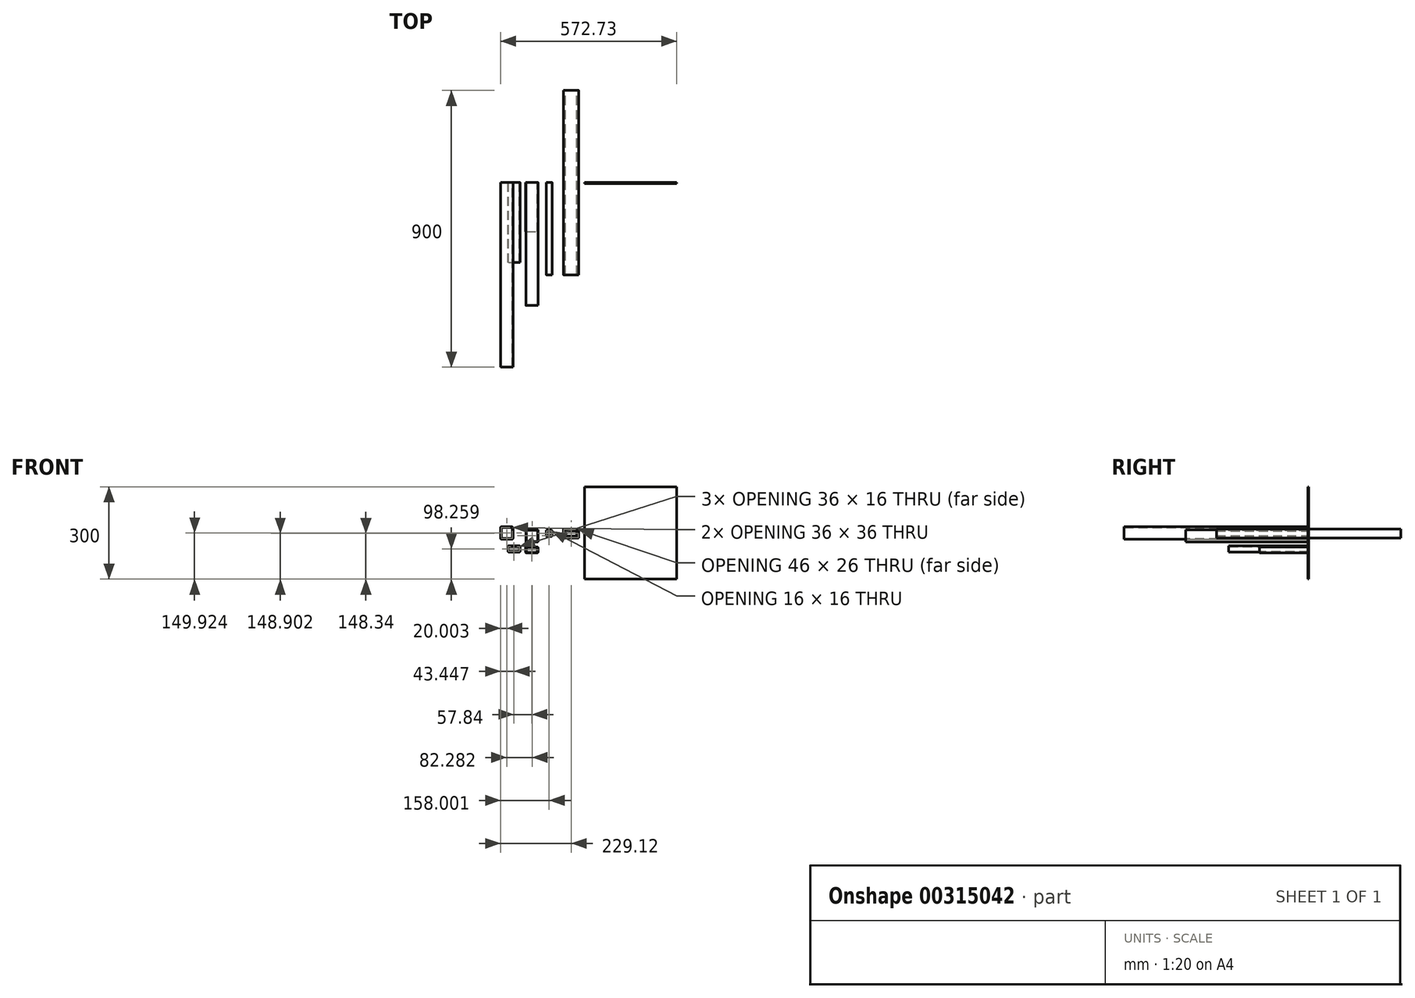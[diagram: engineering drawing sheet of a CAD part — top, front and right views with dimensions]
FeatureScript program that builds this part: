
annotation { "Feature Type Name" : "Feature", "Feature Type Description" : "" }
export const myFeature = defineFeature(function(context is Context, id is Id, definition is map)
    precondition{}
    {
        {
            var Q0;
            Q0=qCreatedBy(makeId("Front.planeOp"),FACE);
            var sketch = newSketch(context, id + "F0", { "sketchPlane" : qUnion([Q0])});
            skLineSegment(sketch, "E0.bottom", {"start": v(22.5, 15) * mm, "end": v(-22.5, 15) * mm});
            skLineSegment(sketch, "E0.top", {"start": v(22.5, -15) * mm, "end": v(-22.5, -15) * mm});
            skLineSegment(sketch, "E0.left", {"start": v(25, 12.5) * mm, "end": v(25, -12.5) * mm});
            skLineSegment(sketch, "E0.right", {"start": v(-25, 12.5) * mm, "end": v(-25, -12.5) * mm});
            skPoint(sketch, "E0.middle", {"position": v(0, 0) * mm});
            skPoint(sketch, "E1.visualSharp", {"position": v(-25, 15) * mm});
            skArc(sketch, "E1.filletArc", {"start": v(-22.5, 15) * mm, "mid": v(-24.27, 14.27) * mm, "end": v(-25, 12.5) * mm});
            skPoint(sketch, "E2.visualSharp", {"position": v(25, 15) * mm});
            skArc(sketch, "E2.filletArc", {"start": v(25, 12.5) * mm, "mid": v(24.27, 14.27) * mm, "end": v(22.5, 15) * mm});
            skPoint(sketch, "E3.visualSharp", {"position": v(25, -15) * mm});
            skArc(sketch, "E3.filletArc", {"start": v(22.5, -15) * mm, "mid": v(24.27, -14.27) * mm, "end": v(25, -12.5) * mm});
            skPoint(sketch, "E4.visualSharp", {"position": v(-25, -15) * mm});
            skArc(sketch, "E4.filletArc", {"start": v(-25, -12.5) * mm, "mid": v(-24.27, -14.27) * mm, "end": v(-22.5, -15) * mm});
            skLineSegment(sketch, "E5.0", {"start": v(22.5, 13) * mm, "end": v(-22.5, 13) * mm});
            skArc(sketch, "E5.1", {"start": v(23, 12.5) * mm, "mid": v(22.85, 12.85) * mm, "end": v(22.5, 13) * mm});
            skArc(sketch, "E5.2", {"start": v(-22.5, 13) * mm, "mid": v(-22.85, 12.85) * mm, "end": v(-23, 12.5) * mm});
            skLineSegment(sketch, "E5.3", {"start": v(23, 12.5) * mm, "end": v(23, -12.5) * mm});
            skLineSegment(sketch, "E5.4", {"start": v(-23, 12.5) * mm, "end": v(-23, -12.5) * mm});
            skArc(sketch, "E5.5", {"start": v(-23, -12.5) * mm, "mid": v(-22.85, -12.85) * mm, "end": v(-22.5, -13) * mm});
            skLineSegment(sketch, "E5.6", {"start": v(22.5, -13) * mm, "end": v(-22.5, -13) * mm});
            skArc(sketch, "E5.7", {"start": v(22.5, -13) * mm, "mid": v(22.85, -12.85) * mm, "end": v(23, -12.5) * mm});
            skSolve(sketch);
        }
        {
            var Q0;
            Q0 = qSketchRegion(id + "F0", true);
            extrude(context, id + "F1", {"entities" : qUnion([Q0]), "endBound" : BoundingType.SYMMETRIC, "depth" : 600 * mm});
        }
        {
            var Q0;
            Q0=qCreatedBy(makeId("Front.planeOp"),FACE);
            var sketch = newSketch(context, id + "F2", { "sketchPlane" : qUnion([Q0])});
            skLineSegment(sketch, "E6.bottom", {"start": v(-17.5, 10) * mm, "end": v(17.5, 10) * mm});
            skLineSegment(sketch, "E6.top", {"start": v(-17.5, -10) * mm, "end": v(17.5, -10) * mm});
            skLineSegment(sketch, "E6.left", {"start": v(-20, 7.5) * mm, "end": v(-20, -7.5) * mm});
            skLineSegment(sketch, "E6.right", {"start": v(20, 7.5) * mm, "end": v(20, -7.5) * mm});
            skPoint(sketch, "E6.middle", {"position": v(0, 0) * mm});
            skPoint(sketch, "E7.visualSharp", {"position": v(-20, 10) * mm});
            skArc(sketch, "E7.filletArc", {"start": v(-17.5, 10) * mm, "mid": v(-19.27, 9.27) * mm, "end": v(-20, 7.5) * mm});
            skPoint(sketch, "E8.visualSharp", {"position": v(20, 10) * mm});
            skArc(sketch, "E8.filletArc", {"start": v(20, 7.5) * mm, "mid": v(19.27, 9.27) * mm, "end": v(17.5, 10) * mm});
            skPoint(sketch, "E9.visualSharp", {"position": v(20, -10) * mm});
            skArc(sketch, "E9.filletArc", {"start": v(17.5, -10) * mm, "mid": v(19.27, -9.27) * mm, "end": v(20, -7.5) * mm});
            skPoint(sketch, "E10.visualSharp", {"position": v(-20, -10) * mm});
            skArc(sketch, "E10.filletArc", {"start": v(-20, -7.5) * mm, "mid": v(-19.27, -9.27) * mm, "end": v(-17.5, -10) * mm});
            skArc(sketch, "E11.0", {"start": v(-17.5, 8) * mm, "mid": v(-17.85, 7.85) * mm, "end": v(-18, 7.5) * mm});
            skLineSegment(sketch, "E11.1", {"start": v(-18, 7.5) * mm, "end": v(-18, -7.5) * mm});
            skLineSegment(sketch, "E11.2", {"start": v(-17.5, 8) * mm, "end": v(17.5, 8) * mm});
            skArc(sketch, "E11.3", {"start": v(-18, -7.5) * mm, "mid": v(-17.85, -7.85) * mm, "end": v(-17.5, -8) * mm});
            skArc(sketch, "E11.4", {"start": v(18, 7.5) * mm, "mid": v(17.85, 7.85) * mm, "end": v(17.5, 8) * mm});
            skLineSegment(sketch, "E11.5", {"start": v(18, 7.5) * mm, "end": v(18, -7.5) * mm});
            skArc(sketch, "E11.6", {"start": v(17.5, -8) * mm, "mid": v(17.85, -7.85) * mm, "end": v(18, -7.5) * mm});
            skLineSegment(sketch, "E11.7", {"start": v(-17.5, -8) * mm, "end": v(17.5, -8) * mm});
            skSolve(sketch);
        }
        {
            var Q0;
            Q0 = qSketchRegion(id + "F2", true);
            extrude(context, id + "F3", {"entities" : qUnion([Q0]), "endBound" : BoundingType.SYMMETRIC, "depth" : 600 * mm});
        }
        {
            var Q0;
            Q0=qCreatedBy(makeId("Front.planeOp"),FACE);
            var sketch = newSketch(context, id + "F4", { "sketchPlane" : qUnion([Q0])});
            skLineSegment(sketch, "E12.bottom", {"start": v(-144.33, 12.36) * mm, "end": v(-109.33, 12.36) * mm});
            skLineSegment(sketch, "E12.top", {"start": v(-144.33, -27.64) * mm, "end": v(-109.33, -27.64) * mm});
            skLineSegment(sketch, "E12.left", {"start": v(-146.83, 9.86) * mm, "end": v(-146.83, -25.14) * mm});
            skLineSegment(sketch, "E12.right", {"start": v(-106.83, 9.86) * mm, "end": v(-106.83, -25.14) * mm});
            skPoint(sketch, "E12.middle", {"position": v(-126.83, -7.64) * mm});
            skPoint(sketch, "E13.visualSharp", {"position": v(-146.83, 12.36) * mm});
            skArc(sketch, "E13.filletArc", {"start": v(-144.33, 12.36) * mm, "mid": v(-146.1, 11.63) * mm, "end": v(-146.83, 9.86) * mm});
            skPoint(sketch, "E14.visualSharp", {"position": v(-106.83, 12.36) * mm});
            skArc(sketch, "E14.filletArc", {"start": v(-106.83, 9.86) * mm, "mid": v(-107.57, 11.63) * mm, "end": v(-109.33, 12.36) * mm});
            skPoint(sketch, "E15.visualSharp", {"position": v(-106.83, -27.64) * mm});
            skArc(sketch, "E15.filletArc", {"start": v(-109.33, -27.64) * mm, "mid": v(-107.57, -26.9) * mm, "end": v(-106.83, -25.14) * mm});
            skPoint(sketch, "E16.visualSharp", {"position": v(-146.83, -27.64) * mm});
            skArc(sketch, "E16.filletArc", {"start": v(-146.83, -25.14) * mm, "mid": v(-146.1, -26.9) * mm, "end": v(-144.33, -27.64) * mm});
            skArc(sketch, "E17.0", {"start": v(-144.33, 10.36) * mm, "mid": v(-144.69, 10.21) * mm, "end": v(-144.83, 9.86) * mm});
            skLineSegment(sketch, "E17.1", {"start": v(-144.83, 9.86) * mm, "end": v(-144.83, -25.14) * mm});
            skLineSegment(sketch, "E17.2", {"start": v(-144.33, 10.36) * mm, "end": v(-109.33, 10.36) * mm});
            skArc(sketch, "E17.3", {"start": v(-144.83, -25.14) * mm, "mid": v(-144.69, -25.5) * mm, "end": v(-144.33, -25.64) * mm});
            skArc(sketch, "E17.4", {"start": v(-108.83, 9.86) * mm, "mid": v(-108.98, 10.21) * mm, "end": v(-109.33, 10.36) * mm});
            skLineSegment(sketch, "E17.5", {"start": v(-108.83, 9.86) * mm, "end": v(-108.83, -25.14) * mm});
            skArc(sketch, "E17.6", {"start": v(-109.33, -25.64) * mm, "mid": v(-108.98, -25.5) * mm, "end": v(-108.83, -25.14) * mm});
            skLineSegment(sketch, "E17.7", {"start": v(-144.33, -25.64) * mm, "end": v(-109.33, -25.64) * mm});
            skSolve(sketch);
        }
        {
            var Q0;
            Q0=qCreatedBy(makeId("Front.planeOp"),FACE);
            var sketch = newSketch(context, id + "F5", { "sketchPlane" : qUnion([Q0])});
            skLineSegment(sketch, "E18.bottom", {"start": v(-78.62, 10.56) * mm, "end": v(-63.62, 10.56) * mm});
            skLineSegment(sketch, "E18.top", {"start": v(-78.62, -9.44) * mm, "end": v(-63.62, -9.44) * mm});
            skLineSegment(sketch, "E18.left", {"start": v(-81.12, 8.06) * mm, "end": v(-81.12, -6.94) * mm});
            skLineSegment(sketch, "E18.right", {"start": v(-61.12, 8.06) * mm, "end": v(-61.12, -6.94) * mm});
            skPoint(sketch, "E19.visualSharp", {"position": v(-81.12, 10.56) * mm});
            skArc(sketch, "E19.filletArc", {"start": v(-78.62, 10.56) * mm, "mid": v(-80.39, 9.83) * mm, "end": v(-81.12, 8.06) * mm});
            skPoint(sketch, "E20.visualSharp", {"position": v(-61.12, 10.56) * mm});
            skArc(sketch, "E20.filletArc", {"start": v(-61.12, 8.06) * mm, "mid": v(-61.85, 9.83) * mm, "end": v(-63.62, 10.56) * mm});
            skPoint(sketch, "E21.visualSharp", {"position": v(-61.12, -9.44) * mm});
            skArc(sketch, "E21.filletArc", {"start": v(-63.62, -9.44) * mm, "mid": v(-61.85, -8.7) * mm, "end": v(-61.12, -6.94) * mm});
            skPoint(sketch, "E22.visualSharp", {"position": v(-81.12, -9.44) * mm});
            skArc(sketch, "E22.filletArc", {"start": v(-81.12, -6.94) * mm, "mid": v(-80.39, -8.7) * mm, "end": v(-78.62, -9.44) * mm});
            skArc(sketch, "E23.0", {"start": v(-78.62, 8.56) * mm, "mid": v(-78.97, 8.42) * mm, "end": v(-79.12, 8.06) * mm});
            skLineSegment(sketch, "E23.1", {"start": v(-79.12, 8.06) * mm, "end": v(-79.12, -6.94) * mm});
            skLineSegment(sketch, "E23.2", {"start": v(-78.62, 8.56) * mm, "end": v(-63.62, 8.56) * mm});
            skArc(sketch, "E23.3", {"start": v(-79.12, -6.94) * mm, "mid": v(-78.97, -7.3) * mm, "end": v(-78.62, -7.44) * mm});
            skArc(sketch, "E23.4", {"start": v(-63.12, 8.06) * mm, "mid": v(-63.27, 8.42) * mm, "end": v(-63.62, 8.56) * mm});
            skLineSegment(sketch, "E23.5", {"start": v(-63.12, 8.06) * mm, "end": v(-63.12, -6.94) * mm});
            skArc(sketch, "E23.6", {"start": v(-63.62, -7.44) * mm, "mid": v(-63.27, -7.3) * mm, "end": v(-63.12, -6.94) * mm});
            skLineSegment(sketch, "E23.7", {"start": v(-78.62, -7.44) * mm, "end": v(-63.62, -7.44) * mm});
            skSolve(sketch);
        }
        {
            var Q0;
            Q0 = qSketchRegion(id + "F5", true);
            extrude(context, id + "F6", {"entities" : qUnion([Q0]), "depth" : 300 * mm});
        }
        {
            var Q0;
            Q0=qCreatedBy(makeId("Front.planeOp"),FACE);
            var sketch = newSketch(context, id + "F7", { "sketchPlane" : qUnion([Q0])});
            skLineSegment(sketch, "E24.bottom", {"start": v(-145.33, -43.44) * mm, "end": v(-110.33, -43.44) * mm});
            skLineSegment(sketch, "E24.top", {"start": v(-145.33, -63.44) * mm, "end": v(-110.33, -63.44) * mm});
            skLineSegment(sketch, "E24.left", {"start": v(-147.83, -45.94) * mm, "end": v(-147.83, -60.94) * mm});
            skLineSegment(sketch, "E24.right", {"start": v(-107.83, -45.94) * mm, "end": v(-107.83, -60.94) * mm});
            skPoint(sketch, "E24.middle", {"position": v(-127.83, -53.44) * mm});
            skPoint(sketch, "E25.visualSharp", {"position": v(-147.83, -43.44) * mm});
            skArc(sketch, "E25.filletArc", {"start": v(-145.33, -43.44) * mm, "mid": v(-147.1, -44.17) * mm, "end": v(-147.83, -45.94) * mm});
            skPoint(sketch, "E26.visualSharp", {"position": v(-107.83, -43.44) * mm});
            skArc(sketch, "E26.filletArc", {"start": v(-107.83, -45.94) * mm, "mid": v(-108.57, -44.17) * mm, "end": v(-110.33, -43.44) * mm});
            skPoint(sketch, "E27.visualSharp", {"position": v(-107.83, -63.44) * mm});
            skArc(sketch, "E27.filletArc", {"start": v(-110.33, -63.44) * mm, "mid": v(-108.57, -62.7) * mm, "end": v(-107.83, -60.94) * mm});
            skPoint(sketch, "E28.visualSharp", {"position": v(-147.83, -63.44) * mm});
            skArc(sketch, "E28.filletArc", {"start": v(-147.83, -60.94) * mm, "mid": v(-147.1, -62.7) * mm, "end": v(-145.33, -63.44) * mm});
            skArc(sketch, "E29.0", {"start": v(-145.33, -45.44) * mm, "mid": v(-145.69, -45.59) * mm, "end": v(-145.83, -45.94) * mm});
            skLineSegment(sketch, "E29.1", {"start": v(-145.83, -45.94) * mm, "end": v(-145.83, -60.94) * mm});
            skLineSegment(sketch, "E29.2", {"start": v(-145.33, -45.44) * mm, "end": v(-110.33, -45.44) * mm});
            skArc(sketch, "E29.3", {"start": v(-145.83, -60.94) * mm, "mid": v(-145.69, -61.3) * mm, "end": v(-145.33, -61.44) * mm});
            skArc(sketch, "E29.4", {"start": v(-109.83, -45.94) * mm, "mid": v(-109.98, -45.59) * mm, "end": v(-110.33, -45.44) * mm});
            skLineSegment(sketch, "E29.5", {"start": v(-109.83, -45.94) * mm, "end": v(-109.83, -60.94) * mm});
            skArc(sketch, "E29.6", {"start": v(-110.33, -61.44) * mm, "mid": v(-109.98, -61.3) * mm, "end": v(-109.83, -60.94) * mm});
            skLineSegment(sketch, "E29.7", {"start": v(-145.33, -61.44) * mm, "end": v(-110.33, -61.44) * mm});
            skSolve(sketch);
        }
        {
            var Q0;
            Q0 = qSketchRegion(id + "F7", true);
            extrude(context, id + "F8", {"entities" : qUnion([Q0]), "depth" : 160 * mm});
        }
        {
            var Q0;
            Q0=qCreatedBy(makeId("Front.planeOp"),FACE);
            var sketch = newSketch(context, id + "F9", { "sketchPlane" : qUnion([Q0])});
            skLineSegment(sketch, "E30.bottom", {"start": v(43.61, 151.66) * mm, "end": v(343.61, 151.66) * mm});
            skLineSegment(sketch, "E30.top", {"start": v(43.61, -148.34) * mm, "end": v(343.61, -148.34) * mm});
            skLineSegment(sketch, "E30.left", {"start": v(43.61, 151.66) * mm, "end": v(43.61, -148.34) * mm});
            skLineSegment(sketch, "E30.right", {"start": v(343.61, 151.66) * mm, "end": v(343.61, -148.34) * mm});
            skSolve(sketch);
        }
        {
            var Q0;
            Q0 = qSketchRegion(id + "F9", true);
            extrude(context, id + "F10", {"entities" : qUnion([Q0]), "depth" : 3 * mm});
        }
        {
            var Q0;
            Q0=qCreatedBy(makeId("Front.planeOp"),FACE);
            var sketch = newSketch(context, id + "F11", { "sketchPlane" : qUnion([Q0])});
            skLineSegment(sketch, "E31.bottom", {"start": v(-203.17, -40.08) * mm, "end": v(-168.17, -40.08) * mm});
            skLineSegment(sketch, "E31.top", {"start": v(-203.17, -60.08) * mm, "end": v(-168.17, -60.08) * mm});
            skLineSegment(sketch, "E31.left", {"start": v(-205.67, -42.58) * mm, "end": v(-205.67, -57.58) * mm});
            skLineSegment(sketch, "E31.right", {"start": v(-165.67, -42.58) * mm, "end": v(-165.67, -57.58) * mm});
            skPoint(sketch, "E31.middle", {"position": v(-185.67, -50.08) * mm});
            skPoint(sketch, "E32.visualSharp", {"position": v(-205.67, -40.08) * mm});
            skArc(sketch, "E32.filletArc", {"start": v(-203.17, -40.08) * mm, "mid": v(-204.94, -40.81) * mm, "end": v(-205.67, -42.58) * mm});
            skPoint(sketch, "E33.visualSharp", {"position": v(-165.67, -40.08) * mm});
            skArc(sketch, "E33.filletArc", {"start": v(-165.67, -42.58) * mm, "mid": v(-166.4, -40.81) * mm, "end": v(-168.17, -40.08) * mm});
            skPoint(sketch, "E34.visualSharp", {"position": v(-165.67, -60.08) * mm});
            skArc(sketch, "E34.filletArc", {"start": v(-168.17, -60.08) * mm, "mid": v(-166.4, -59.35) * mm, "end": v(-165.67, -57.58) * mm});
            skPoint(sketch, "E35.visualSharp", {"position": v(-205.67, -60.08) * mm});
            skArc(sketch, "E35.filletArc", {"start": v(-205.67, -57.58) * mm, "mid": v(-204.94, -59.35) * mm, "end": v(-203.17, -60.08) * mm});
            skArc(sketch, "E36.0", {"start": v(-203.17, -42.08) * mm, "mid": v(-203.53, -42.23) * mm, "end": v(-203.67, -42.58) * mm});
            skLineSegment(sketch, "E36.1", {"start": v(-203.67, -42.58) * mm, "end": v(-203.67, -57.58) * mm});
            skLineSegment(sketch, "E36.2", {"start": v(-203.17, -42.08) * mm, "end": v(-168.17, -42.08) * mm});
            skArc(sketch, "E36.3", {"start": v(-203.67, -57.58) * mm, "mid": v(-203.53, -57.93) * mm, "end": v(-203.17, -58.08) * mm});
            skArc(sketch, "E36.4", {"start": v(-167.67, -42.58) * mm, "mid": v(-167.82, -42.23) * mm, "end": v(-168.17, -42.08) * mm});
            skLineSegment(sketch, "E36.5", {"start": v(-167.67, -42.58) * mm, "end": v(-167.67, -57.58) * mm});
            skArc(sketch, "E36.6", {"start": v(-168.17, -58.08) * mm, "mid": v(-167.82, -57.93) * mm, "end": v(-167.67, -57.58) * mm});
            skLineSegment(sketch, "E36.7", {"start": v(-203.17, -58.08) * mm, "end": v(-168.17, -58.08) * mm});
            skSolve(sketch);
        }
        {
            var Q0;
            Q0 = qSketchRegion(id + "F11", true);
            extrude(context, id + "F12", {"entities" : qUnion([Q0]), "depth" : 260 * mm});
        }
        {
            var Q0;
            Q0=qCreatedBy(makeId("Front.planeOp"),FACE);
            var sketch = newSketch(context, id + "F13", { "sketchPlane" : qUnion([Q0])});
            skLineSegment(sketch, "E37.bottom", {"start": v(-226.62, 21.58) * mm, "end": v(-191.62, 21.58) * mm});
            skLineSegment(sketch, "E37.top", {"start": v(-226.62, -18.42) * mm, "end": v(-191.62, -18.42) * mm});
            skLineSegment(sketch, "E37.left", {"start": v(-229.12, 19.08) * mm, "end": v(-229.12, -15.92) * mm});
            skLineSegment(sketch, "E37.right", {"start": v(-189.12, 19.08) * mm, "end": v(-189.12, -15.92) * mm});
            skPoint(sketch, "E37.middle", {"position": v(-209.12, 1.58) * mm});
            skPoint(sketch, "E38.visualSharp", {"position": v(-229.12, 21.58) * mm});
            skArc(sketch, "E38.filletArc", {"start": v(-226.62, 21.58) * mm, "mid": v(-228.38, 20.85) * mm, "end": v(-229.12, 19.08) * mm});
            skPoint(sketch, "E39.visualSharp", {"position": v(-189.12, 21.58) * mm});
            skArc(sketch, "E39.filletArc", {"start": v(-189.12, 19.08) * mm, "mid": v(-189.85, 20.85) * mm, "end": v(-191.62, 21.58) * mm});
            skPoint(sketch, "E40.visualSharp", {"position": v(-189.12, -18.42) * mm});
            skArc(sketch, "E40.filletArc", {"start": v(-191.62, -18.42) * mm, "mid": v(-189.85, -17.68) * mm, "end": v(-189.12, -15.92) * mm});
            skPoint(sketch, "E41.visualSharp", {"position": v(-229.12, -18.42) * mm});
            skArc(sketch, "E41.filletArc", {"start": v(-229.12, -15.92) * mm, "mid": v(-228.38, -17.68) * mm, "end": v(-226.62, -18.42) * mm});
            skArc(sketch, "E42.0", {"start": v(-226.62, 19.58) * mm, "mid": v(-226.97, 19.44) * mm, "end": v(-227.12, 19.08) * mm});
            skLineSegment(sketch, "E42.1", {"start": v(-227.12, 19.08) * mm, "end": v(-227.12, -15.92) * mm});
            skLineSegment(sketch, "E42.2", {"start": v(-226.62, 19.58) * mm, "end": v(-191.62, 19.58) * mm});
            skArc(sketch, "E42.3", {"start": v(-227.12, -15.92) * mm, "mid": v(-226.97, -16.27) * mm, "end": v(-226.62, -16.42) * mm});
            skArc(sketch, "E42.4", {"start": v(-191.12, 19.08) * mm, "mid": v(-191.26, 19.44) * mm, "end": v(-191.62, 19.58) * mm});
            skLineSegment(sketch, "E42.5", {"start": v(-191.12, 19.08) * mm, "end": v(-191.12, -15.92) * mm});
            skArc(sketch, "E42.6", {"start": v(-191.62, -16.42) * mm, "mid": v(-191.26, -16.27) * mm, "end": v(-191.12, -15.92) * mm});
            skLineSegment(sketch, "E42.7", {"start": v(-226.62, -16.42) * mm, "end": v(-191.62, -16.42) * mm});
            skSolve(sketch);
        }
        {
            var Q0;
            Q0 = qSketchRegion(id + "F13", true);
            extrude(context, id + "F14", {"entities" : qUnion([Q0]), "depth" : 600 * mm});
        }
        {
            var Q0;
            Q0 = qSketchRegion(id + "F4", true);
            extrude(context, id + "F15", {"entities" : qUnion([Q0]), "depth" : 400 * mm});
        }
    });
